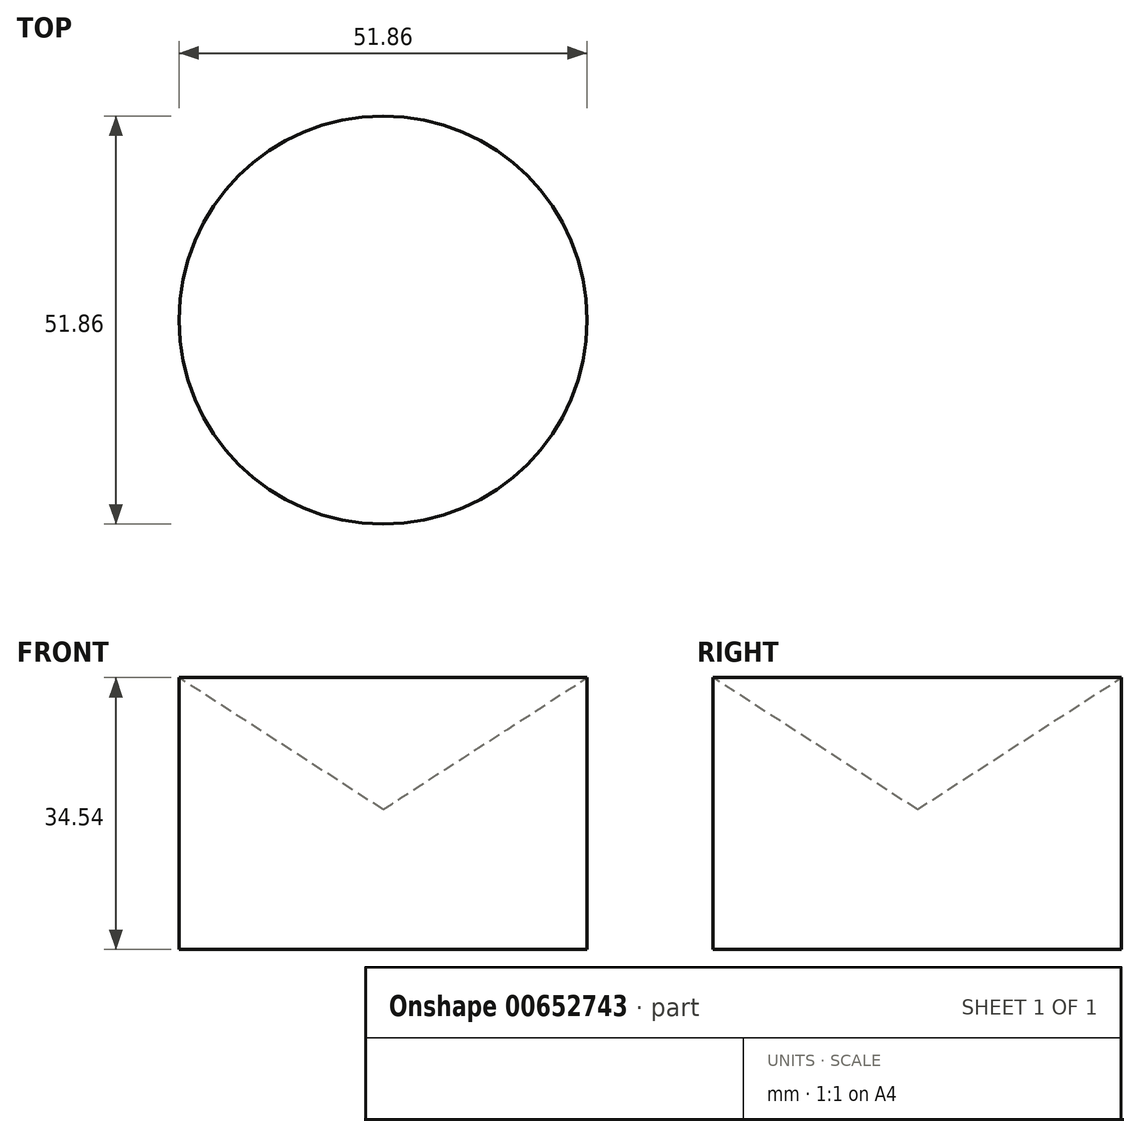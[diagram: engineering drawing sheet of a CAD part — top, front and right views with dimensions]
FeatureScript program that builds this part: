
annotation { "Feature Type Name" : "Feature", "Feature Type Description" : "" }
export const myFeature = defineFeature(function(context is Context, id is Id, definition is map)
    precondition{}
    {
        {
            var Q0;
            Q0=qCreatedBy(makeId("Front.planeOp"),FACE);
            var sketch = newSketch(context, id + "F0", { "sketchPlane" : qUnion([Q0])});
            skLineSegment(sketch, "E0", {"start": v(0, 0) * mm, "end": v(0, 17.8) * mm});
            skLineSegment(sketch, "E1", {"start": v(0, 17.8) * mm, "end": v(25.93, 34.54) * mm});
            skLineSegment(sketch, "E2", {"start": v(25.93, 34.54) * mm, "end": v(25.93, 0) * mm});
            skLineSegment(sketch, "E3", {"start": v(25.93, 0) * mm, "end": v(0, 0) * mm});
            skSolve(sketch);
        }
        {
            var Q0;
            Q0=makeQuery(id+"F0.imprint","IMPRINT",FACE,{"disambiguationData":[TD([[makeQuery(id+"F0.imprint","IMPRINT",EDGE,{"derivedFrom":sQuery(id+"F0.wireOp",EDGE,"E0")}),-1.0]])]});
            var Q1;
            Q1=sQuery(id+"F0.wireOp",EDGE,"E0");
            revolve(context, id + "F1", {"entities" : qUnion([Q0]), "axis" : qUnion([Q1]), "revolveType" : RevolveType.FULL});
        }
    });
